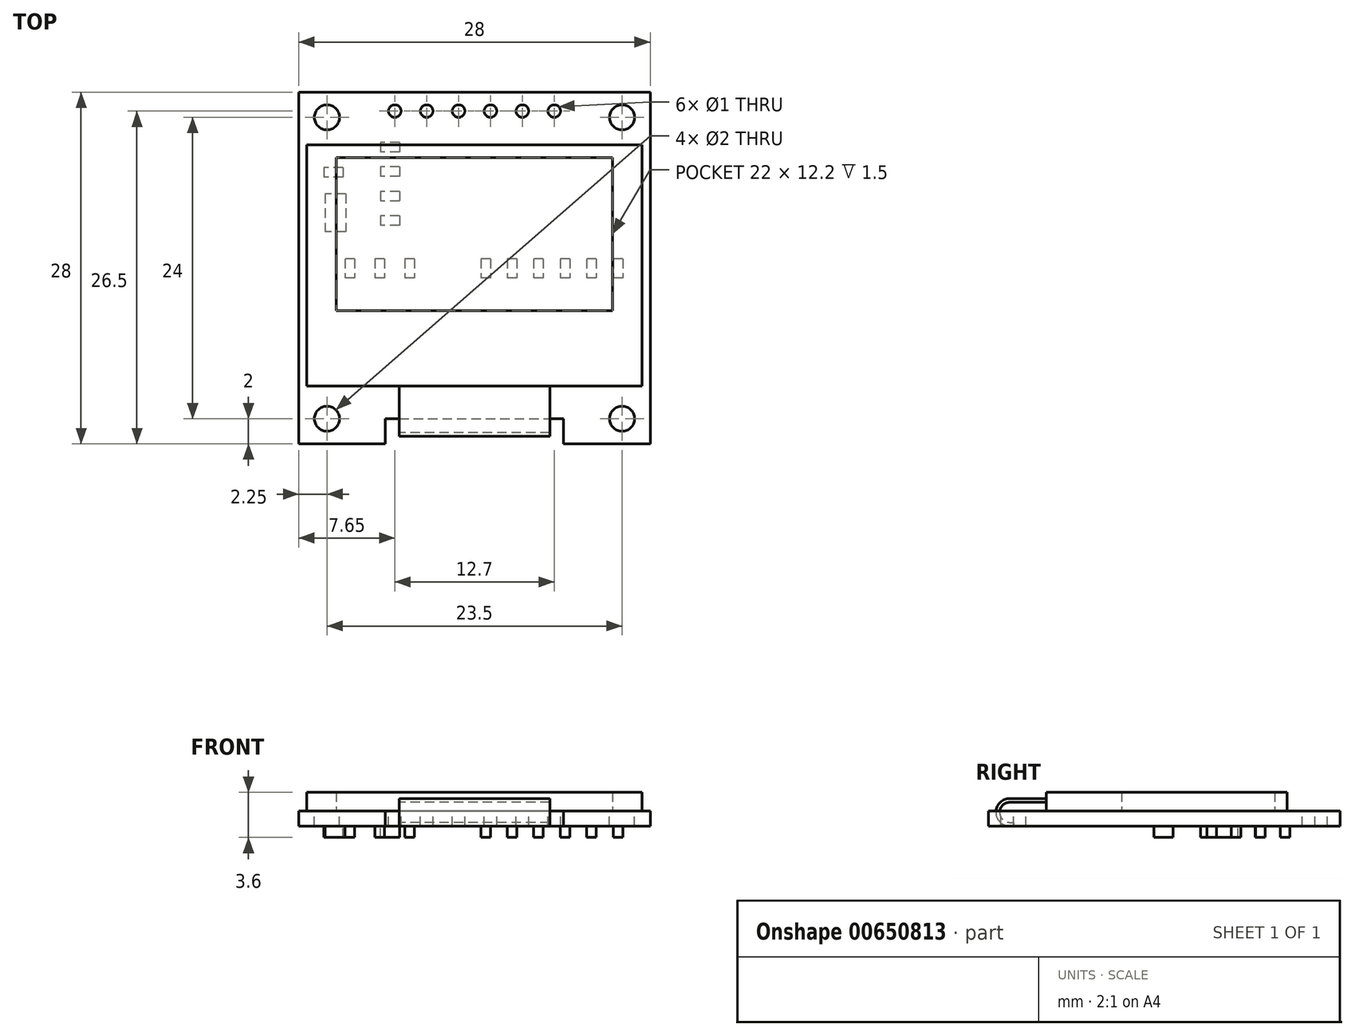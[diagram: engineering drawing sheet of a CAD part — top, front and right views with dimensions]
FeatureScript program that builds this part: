
annotation { "Feature Type Name" : "Feature", "Feature Type Description" : "" }
export const myFeature = defineFeature(function(context is Context, id is Id, definition is map)
    precondition{}
    {
        {
            var Q0;
            Q0=qCreatedBy(makeId("Top.planeOp"),FACE);
            var sketch = newSketch(context, id + "F0", { "sketchPlane" : qUnion([Q0])});
            skLineSegment(sketch, "E0.bottom", {"start": v(14, 28) * mm, "end": v(-14, 28) * mm});
            skLineSegment(sketch, "E0.top", {"start": v(14, 0) * mm, "end": v(7.1, 0) * mm});
            skLineSegment(sketch, "E0.left", {"start": v(14, 28) * mm, "end": v(14, 0) * mm});
            skLineSegment(sketch, "E0.right", {"start": v(-14, 28) * mm, "end": v(-14, 0) * mm});
            skPoint(sketch, "E0.middle", {"position": v(0, 14) * mm});
            skLineSegment(sketch, "E1", {"start": v(-7.1, 2) * mm, "end": v(7.1, 2) * mm});
            skPoint(sketch, "E2", {"position": v(0, 2) * mm});
            skLineSegment(sketch, "E3", {"start": v(7.1, 2) * mm, "end": v(7.1, 0) * mm});
            skLineSegment(sketch, "E4", {"start": v(-7.1, 2) * mm, "end": v(-7.1, 0) * mm});
            skLineSegment(sketch, "E5.trimOffspring", {"start": v(-7.1, 0) * mm, "end": v(-14, 0) * mm});
            skLineSegment(sketch, "E6.bottom", {"start": v(-11.75, 26) * mm, "end": v(11.75, 26) * mm, "construction": true});
            skLineSegment(sketch, "E6.top", {"start": v(-11.75, 2) * mm, "end": v(11.75, 2) * mm, "construction": true});
            skLineSegment(sketch, "E6.left", {"start": v(-11.75, 26) * mm, "end": v(-11.75, 2) * mm, "construction": true});
            skLineSegment(sketch, "E6.right", {"start": v(11.75, 26) * mm, "end": v(11.75, 2) * mm, "construction": true});
            skCircle(sketch, "E7", {"center": v(-11.75, 2) * mm, "radius": 1 * mm});
            skCircle(sketch, "E8", {"center": v(-11.75, 26) * mm, "radius": 1 * mm});
            skCircle(sketch, "E9", {"center": v(11.75, 26) * mm, "radius": 1 * mm});
            skCircle(sketch, "E10", {"center": v(11.75, 2) * mm, "radius": 1 * mm});
            skCircle(sketch, "E11", {"center": v(6.35, 26.5) * mm, "radius": 0.5 * mm});
            skCircle(sketch, "E12.1.0.0", {"center": v(3.8, 26.5) * mm, "radius": 0.5 * mm});
            skCircle(sketch, "E12.2.0.0", {"center": v(1.27, 26.5) * mm, "radius": 0.5 * mm});
            skCircle(sketch, "E12.3.0.0", {"center": v(-1.27, 26.5) * mm, "radius": 0.5 * mm});
            skLineSegment(sketch, "E12.direction1", {"start": v(6.35, 26.5) * mm, "end": v(3.8, 26.5) * mm, "construction": true});
            skCircle(sketch, "E13.0.4.0", {"center": v(-3.81, 26.5) * mm, "radius": 0.5 * mm});
            skCircle(sketch, "E13.0.5.0", {"center": v(-6.35, 26.5) * mm, "radius": 0.5 * mm});
            skSolve(sketch);
        }
        {
            var Q0;
            Q0=makeQuery(id+"F0.imprint","IMPRINT",FACE,{"disambiguationData":[TD([[makeQuery(id+"F0.imprint","IMPRINT",EDGE,{"derivedFrom":sQuery(id+"F0.wireOp",EDGE,"E0.bottom")}),1.0]])]});
            extrude(context, id + "F1", {"entities" : qUnion([Q0]), "oppositeDirection" : true, "depth" : 1.2 * mm, "offsetDistance" : 25 * mm});
        }
        {
            var Q0;
            Q0=qCreatedBy(makeId("Top.planeOp"),FACE);
            var sketch = newSketch(context, id + "F2", { "sketchPlane" : qUnion([Q0])});
            skLineSegment(sketch, "E14.bottom", {"start": v(-13.35, 23.8) * mm, "end": v(13.35, 23.8) * mm});
            skLineSegment(sketch, "E14.top", {"start": v(-13.35, 4.6) * mm, "end": v(13.35, 4.6) * mm});
            skLineSegment(sketch, "E14.left", {"start": v(-13.35, 23.8) * mm, "end": v(-13.35, 4.6) * mm});
            skLineSegment(sketch, "E14.right", {"start": v(13.35, 23.8) * mm, "end": v(13.35, 4.6) * mm});
            skPoint(sketch, "E14.middle", {"position": v(0, 14.2) * mm});
            skLineSegment(sketch, "E15.bottom", {"start": v(11, 22.8) * mm, "end": v(-11, 22.8) * mm});
            skLineSegment(sketch, "E15.top", {"start": v(11, 10.6) * mm, "end": v(-11, 10.6) * mm});
            skLineSegment(sketch, "E15.left", {"start": v(11, 22.8) * mm, "end": v(11, 10.6) * mm});
            skLineSegment(sketch, "E15.right", {"start": v(-11, 22.8) * mm, "end": v(-11, 10.6) * mm});
            skPoint(sketch, "E15.middle", {"position": v(0, 16.7) * mm});
            skSolve(sketch);
        }
        {
            var Q0;
            Q0=makeQuery(id+"F2.imprint","IMPRINT",FACE,{"disambiguationData":[TD([[makeQuery(id+"F2.imprint","IMPRINT",EDGE,{"derivedFrom":sQuery(id+"F2.wireOp",EDGE,"E14.bottom")}),-1.0]])]});
            extrude(context, id + "F3", {"entities" : qUnion([Q0]), "depth" : 1.5 * mm, "offsetDistance" : 25 * mm});
        }
        {
            var Q0;
            Q0=makeQuery(id+"F2.imprint","IMPRINT",FACE,{"disambiguationData":[TD([[makeQuery(id+"F2.imprint","IMPRINT",EDGE,{"derivedFrom":sQuery(id+"F2.wireOp",EDGE,"E15.bottom")}),1.0]])]});
            var Q1;
            Q1=makeQuery(id+"F3.opExtrude","CAP_FACE",FACE,{"disambiguationData":[OSD([sQuery(id+"F2.wireOp",EDGE,"E14.bottom"),sQuery(id+"F2.wireOp",EDGE,"E14.top"),sQuery(id+"F2.wireOp",EDGE,"E14.left"),sQuery(id+"F2.wireOp",EDGE,"E14.right"),sQuery(id+"F2.wireOp",EDGE,"E15.bottom"),sQuery(id+"F2.wireOp",EDGE,"E15.top"),sQuery(id+"F2.wireOp",EDGE,"E15.left"),sQuery(id+"F2.wireOp",EDGE,"E15.right")])],"isStart":false});
            extrude(context, id + "F4", {"entities" : qUnion([Q0]), "endBound" : BoundingType.UP_TO_SURFACE, "depth" : 25 * mm, "endBoundEntityFace" : qUnion([Q1]), "offsetDistance" : 25 * mm});
        }
        {
            var Q0;
            Q0=qCreatedBy(makeId("Right.planeOp"),FACE);
            var sketch = newSketch(context, id + "F5", { "sketchPlane" : qUnion([Q0])});
            skArc(sketch, "E16", {"start": v(1.7, 1) * mm, "mid": v(0.6, -0.1) * mm, "end": v(1.7, -1.2) * mm});
            skLineSegment(sketch, "E17", {"start": v(1.7, -1.2) * mm, "end": v(2, -1.2) * mm});
            skLineSegment(sketch, "E18", {"start": v(1.7, 1) * mm, "end": v(4.6, 1) * mm});
            skLineSegment(sketch, "E19", {"start": v(4.6, 1) * mm, "end": v(4.6, 0.7) * mm});
            skLineSegment(sketch, "E20", {"start": v(2, -0.9) * mm, "end": v(2, -1.2) * mm});
            skArc(sketch, "E21", {"start": v(1.7, -0.9) * mm, "mid": v(0.9, -0.1) * mm, "end": v(1.7, 0.7) * mm});
            skLineSegment(sketch, "E22", {"start": v(1.7, 0.7) * mm, "end": v(4.6, 0.7) * mm});
            skLineSegment(sketch, "E23", {"start": v(1.7, -0.9) * mm, "end": v(2, -0.9) * mm});
            skSolve(sketch);
        }
        {
            var Q0;
            Q0=makeQuery(id+"F5.imprint","IMPRINT",FACE,{"disambiguationData":[TD([[makeQuery(id+"F5.imprint","IMPRINT",EDGE,{"derivedFrom":sQuery(id+"F5.wireOp",EDGE,"E16")}),1.0]])]});
            extrude(context, id + "F6", {"entities" : qUnion([Q0]), "operationType" : NewBodyOperationType.ADD, "depth" : 12 * mm, "offsetDistance" : 25 * mm, "symmetric" : true});
        }
        {
            var Q0;
            Q0=makeQuery(id+"F1.opExtrude","CAP_FACE",FACE,{"disambiguationData":[OSD([sQuery(id+"F0.wireOp",EDGE,"E0.bottom"),sQuery(id+"F0.wireOp",EDGE,"E0.top"),sQuery(id+"F0.wireOp",EDGE,"E0.left"),sQuery(id+"F0.wireOp",EDGE,"E0.right"),sQuery(id+"F0.wireOp",EDGE,"E1"),sQuery(id+"F0.wireOp",EDGE,"E3"),sQuery(id+"F0.wireOp",EDGE,"E4"),sQuery(id+"F0.wireOp",EDGE,"E5.trimOffspring"),sQuery(id+"F0.wireOp",EDGE,"E7"),sQuery(id+"F0.wireOp",EDGE,"E8"),sQuery(id+"F0.wireOp",EDGE,"E9"),sQuery(id+"F0.wireOp",EDGE,"E10"),sQuery(id+"F0.wireOp",EDGE,"E11"),sQuery(id+"F0.wireOp",EDGE,"E12.1.0.0"),sQuery(id+"F0.wireOp",EDGE,"E12.2.0.0"),sQuery(id+"F0.wireOp",EDGE,"E12.3.0.0")])],"isStart":false});
            var sketch = newSketch(context, id + "F7", { "sketchPlane" : qUnion([Q0])});
            skLineSegment(sketch, "E24.bottom", {"start": v(11.8, -14.72) * mm, "end": v(11.04, -14.72) * mm});
            skLineSegment(sketch, "E24.top", {"start": v(11.8, -13.2) * mm, "end": v(11.04, -13.2) * mm});
            skLineSegment(sketch, "E24.left", {"start": v(11.8, -14.72) * mm, "end": v(11.8, -13.2) * mm});
            skLineSegment(sketch, "E24.right", {"start": v(11.04, -14.72) * mm, "end": v(11.04, -13.2) * mm});
            skLineSegment(sketch, "E25.1.0.0", {"start": v(8.93, -14.72) * mm, "end": v(8.93, -13.2) * mm});
            skLineSegment(sketch, "E25.1.0.1", {"start": v(9.7, -14.72) * mm, "end": v(8.93, -14.72) * mm});
            skLineSegment(sketch, "E25.1.0.2", {"start": v(9.7, -14.72) * mm, "end": v(9.7, -13.2) * mm});
            skLineSegment(sketch, "E25.1.0.3", {"start": v(9.7, -13.2) * mm, "end": v(8.93, -13.2) * mm});
            skLineSegment(sketch, "E25.2.0.0", {"start": v(6.82, -14.72) * mm, "end": v(6.82, -13.2) * mm});
            skLineSegment(sketch, "E25.2.0.1", {"start": v(7.58, -14.72) * mm, "end": v(6.82, -14.72) * mm});
            skLineSegment(sketch, "E25.2.0.2", {"start": v(7.58, -14.72) * mm, "end": v(7.58, -13.2) * mm});
            skLineSegment(sketch, "E25.2.0.3", {"start": v(7.58, -13.2) * mm, "end": v(6.82, -13.2) * mm});
            skLineSegment(sketch, "E25.3.0.0", {"start": v(4.72, -14.72) * mm, "end": v(4.72, -13.2) * mm});
            skLineSegment(sketch, "E25.3.0.1", {"start": v(5.48, -14.72) * mm, "end": v(4.72, -14.72) * mm});
            skLineSegment(sketch, "E25.3.0.2", {"start": v(5.48, -14.72) * mm, "end": v(5.48, -13.2) * mm});
            skLineSegment(sketch, "E25.3.0.3", {"start": v(5.48, -13.2) * mm, "end": v(4.72, -13.2) * mm});
            skLineSegment(sketch, "E25.4.0.0", {"start": v(2.6, -14.72) * mm, "end": v(2.6, -13.2) * mm});
            skLineSegment(sketch, "E25.4.0.1", {"start": v(3.37, -14.72) * mm, "end": v(2.6, -14.72) * mm});
            skLineSegment(sketch, "E25.4.0.2", {"start": v(3.37, -14.72) * mm, "end": v(3.37, -13.2) * mm});
            skLineSegment(sketch, "E25.4.0.3", {"start": v(3.37, -13.2) * mm, "end": v(2.6, -13.2) * mm});
            skLineSegment(sketch, "E25.5.0.0", {"start": v(0.5, -14.72) * mm, "end": v(0.5, -13.2) * mm});
            skLineSegment(sketch, "E25.5.0.1", {"start": v(1.26, -14.72) * mm, "end": v(0.5, -14.72) * mm});
            skLineSegment(sketch, "E25.5.0.2", {"start": v(1.26, -14.72) * mm, "end": v(1.26, -13.2) * mm});
            skLineSegment(sketch, "E25.5.0.3", {"start": v(1.26, -13.2) * mm, "end": v(0.5, -13.2) * mm});
            skLineSegment(sketch, "E25.direction1", {"start": v(11.04, -14.72) * mm, "end": v(8.93, -14.72) * mm, "construction": true});
            skLineSegment(sketch, "E26.bottom", {"start": v(-4.8, -14.72) * mm, "end": v(-5.56, -14.72) * mm});
            skLineSegment(sketch, "E26.top", {"start": v(-4.8, -13.2) * mm, "end": v(-5.56, -13.2) * mm});
            skLineSegment(sketch, "E26.left", {"start": v(-5.56, -14.72) * mm, "end": v(-5.56, -13.2) * mm});
            skLineSegment(sketch, "E26.right", {"start": v(-4.8, -14.72) * mm, "end": v(-4.8, -13.2) * mm});
            skLineSegment(sketch, "E27.bottom", {"start": v(-10.25, -19.9) * mm, "end": v(-11.9, -19.9) * mm});
            skLineSegment(sketch, "E27.top", {"start": v(-10.25, -16.9) * mm, "end": v(-11.9, -16.9) * mm});
            skLineSegment(sketch, "E27.left", {"start": v(-10.25, -19.9) * mm, "end": v(-10.25, -16.9) * mm});
            skLineSegment(sketch, "E27.right", {"start": v(-11.9, -19.9) * mm, "end": v(-11.9, -16.9) * mm});
            skLineSegment(sketch, "E28.bottom", {"start": v(-10.48, -22) * mm, "end": v(-12, -22) * mm});
            skLineSegment(sketch, "E28.top", {"start": v(-10.48, -21.24) * mm, "end": v(-12, -21.24) * mm});
            skLineSegment(sketch, "E28.left", {"start": v(-10.48, -22) * mm, "end": v(-10.48, -21.24) * mm});
            skLineSegment(sketch, "E28.right", {"start": v(-12, -22) * mm, "end": v(-12, -21.24) * mm});
            skLineSegment(sketch, "E29.bottom", {"start": v(-5.98, -24) * mm, "end": v(-7.5, -24) * mm});
            skLineSegment(sketch, "E29.top", {"start": v(-5.98, -23.24) * mm, "end": v(-7.5, -23.24) * mm});
            skLineSegment(sketch, "E29.left", {"start": v(-5.98, -24) * mm, "end": v(-5.98, -23.24) * mm});
            skLineSegment(sketch, "E29.right", {"start": v(-7.5, -24) * mm, "end": v(-7.5, -23.24) * mm});
            skLineSegment(sketch, "E30.1.0.0", {"start": v(-7.93, -14.72) * mm, "end": v(-7.93, -13.2) * mm});
            skLineSegment(sketch, "E30.1.0.1", {"start": v(-7.17, -14.72) * mm, "end": v(-7.93, -14.72) * mm});
            skLineSegment(sketch, "E30.1.0.2", {"start": v(-7.17, -14.72) * mm, "end": v(-7.17, -13.2) * mm});
            skLineSegment(sketch, "E30.1.0.3", {"start": v(-7.17, -13.2) * mm, "end": v(-7.93, -13.2) * mm});
            skLineSegment(sketch, "E30.2.0.0", {"start": v(-10.3, -14.72) * mm, "end": v(-10.3, -13.2) * mm});
            skLineSegment(sketch, "E30.2.0.1", {"start": v(-9.54, -14.72) * mm, "end": v(-10.3, -14.72) * mm});
            skLineSegment(sketch, "E30.2.0.2", {"start": v(-9.54, -14.72) * mm, "end": v(-9.54, -13.2) * mm});
            skLineSegment(sketch, "E30.2.0.3", {"start": v(-9.54, -13.2) * mm, "end": v(-10.3, -13.2) * mm});
            skLineSegment(sketch, "E30.direction1", {"start": v(-5.56, -14.72) * mm, "end": v(-7.93, -14.72) * mm, "construction": true});
            skLineSegment(sketch, "E31.1.0.0", {"start": v(-5.98, -22.05) * mm, "end": v(-7.5, -22.05) * mm});
            skLineSegment(sketch, "E31.1.0.1", {"start": v(-7.5, -22.05) * mm, "end": v(-7.5, -21.3) * mm});
            skLineSegment(sketch, "E31.1.0.2", {"start": v(-5.98, -21.3) * mm, "end": v(-7.5, -21.3) * mm});
            skLineSegment(sketch, "E31.1.0.3", {"start": v(-5.98, -22.05) * mm, "end": v(-5.98, -21.3) * mm});
            skLineSegment(sketch, "E31.2.0.0", {"start": v(-5.98, -20.1) * mm, "end": v(-7.5, -20.1) * mm});
            skLineSegment(sketch, "E31.2.0.1", {"start": v(-7.5, -20.1) * mm, "end": v(-7.5, -19.35) * mm});
            skLineSegment(sketch, "E31.2.0.2", {"start": v(-5.98, -19.35) * mm, "end": v(-7.5, -19.35) * mm});
            skLineSegment(sketch, "E31.2.0.3", {"start": v(-5.98, -20.1) * mm, "end": v(-5.98, -19.35) * mm});
            skLineSegment(sketch, "E31.direction1", {"start": v(-7.5, -24) * mm, "end": v(-7.5, -22.05) * mm, "construction": true});
            skLineSegment(sketch, "E32.0.3.0", {"start": v(-5.98, -18.16) * mm, "end": v(-7.5, -18.16) * mm});
            skLineSegment(sketch, "E32.3.3.0", {"start": v(-7.5, -18.16) * mm, "end": v(-7.5, -17.4) * mm});
            skLineSegment(sketch, "E32.6.3.0", {"start": v(-5.98, -17.4) * mm, "end": v(-7.5, -17.4) * mm});
            skLineSegment(sketch, "E32.9.3.0", {"start": v(-5.98, -18.16) * mm, "end": v(-5.98, -17.4) * mm});
            skSolve(sketch);
        }
        {
            var Q0;
            Q0=qSketchRegion(id+"F7",true);
            extrude(context, id + "F8", {"entities" : qUnion([Q0]), "operationType" : NewBodyOperationType.ADD, "depth" : 0.9 * mm, "offsetDistance" : 25 * mm});
        }
    });
